# Revit family: Mixer_Wall_Nero_Bianca
name_source: partatom
category: Plumbing Fixtures
units: mm (PartAtom-declared; Revit-internal decimal feet)

## family parameters
Always vertical = Yes
Cut with Voids When Loaded = Yes
Maintain Annotation Orientation = No
OmniClass Number = 23.31.00.00
Part Type = Normal
Room Calculation Point = No
Round Connector Dimension = Use Diameter
Shared = No
Work Plane-Based = No

## types (6) — shared parameters
Assembly Code = D2010
CW Connection = Yes
HW Connection = Yes
IfcExportAs = IfcSanitaryTerminal
IfcExportType = NOTDEFINED
Manufacturer = Nero
ManufacturerOverallDepth = 175 mm  [stored 0.574147 ft]
ManufacturerOverallHeight = 169.2 mm  [stored 0.555118 ft]
ManufacturerOverallWidth = 50 mm  [stored 0.164042 ft]
ManufacturerURLProductSpecific = https://nerotapware.com.au
ModifiedIssue = 20241210 $
URL = https://nerotapware.com.au
Uniclass2015Code = Pr_40_20_87
Uniclass2015Title = Taps and water supply outlet fittings
Uniclass2015Version = Products v1.35
Vent Connection = No
Waste Connection = No
zero-valued in all types: Default Elevation

## per-type parameters (varying)
| type | BodyMaterial | Description | ManufacturerSpecCode | Model | Type Comments |
| Matte Black (NR321502MB) | Metal_MatteBlack_Nero | Bianca Basin Mixer Straight Spout Matte Black | NR321502MB | NR321502MB | Mixer Set - Wall - Matte Black |
| Brushed Bronze (NR321502BZ) | Metal_Bronze_Nero_Brushed | Bianca Basin Mixer Straight Spout Brushed Bronze | NR321502BZ | NR321502BZ | Mixer Set - Wall - Brushed Bronze |
| Gun Metal (NR321502GM) | Metal_GunMetal_Nero | Bianca Basin Mixer Straight Spout Gun Metal | NR321502GM | NR321502GM | Mixer Set - Wall - Gun Metal |
| Brushed Gold (NR321502BG) | Metal_Gold_Nero_Brushed | Bianca Basin Mixer Straight Spout Brushed Gold | NR321502BG | NR321502BG | Mixer Set - Wall - Brushed Gold |
| Brushed Nickel (NR321502BN) | Metal_Nickel_Nero_Brushed | Bianca Basin Mixer Straight Spout Brushed Nickel | NR321502BN | NR321502BN | Mixer Set - Wall - Brushed Nickel |
| Chrome (NR321502CH) | Metal_Chrome_Nero | Bianca Basin Mixer Straight Spout Chrome | NR321502CH | NR321502CH | Mixer Set - Wall - Chrome |

note: [stored X ft] marks values corroborated as IEEE doubles in the binary element streams (Revit-internal decimal feet)

## geometry (parser evidence)
native form markers: Sweep x2
no freeform markers — native parametric forms only
